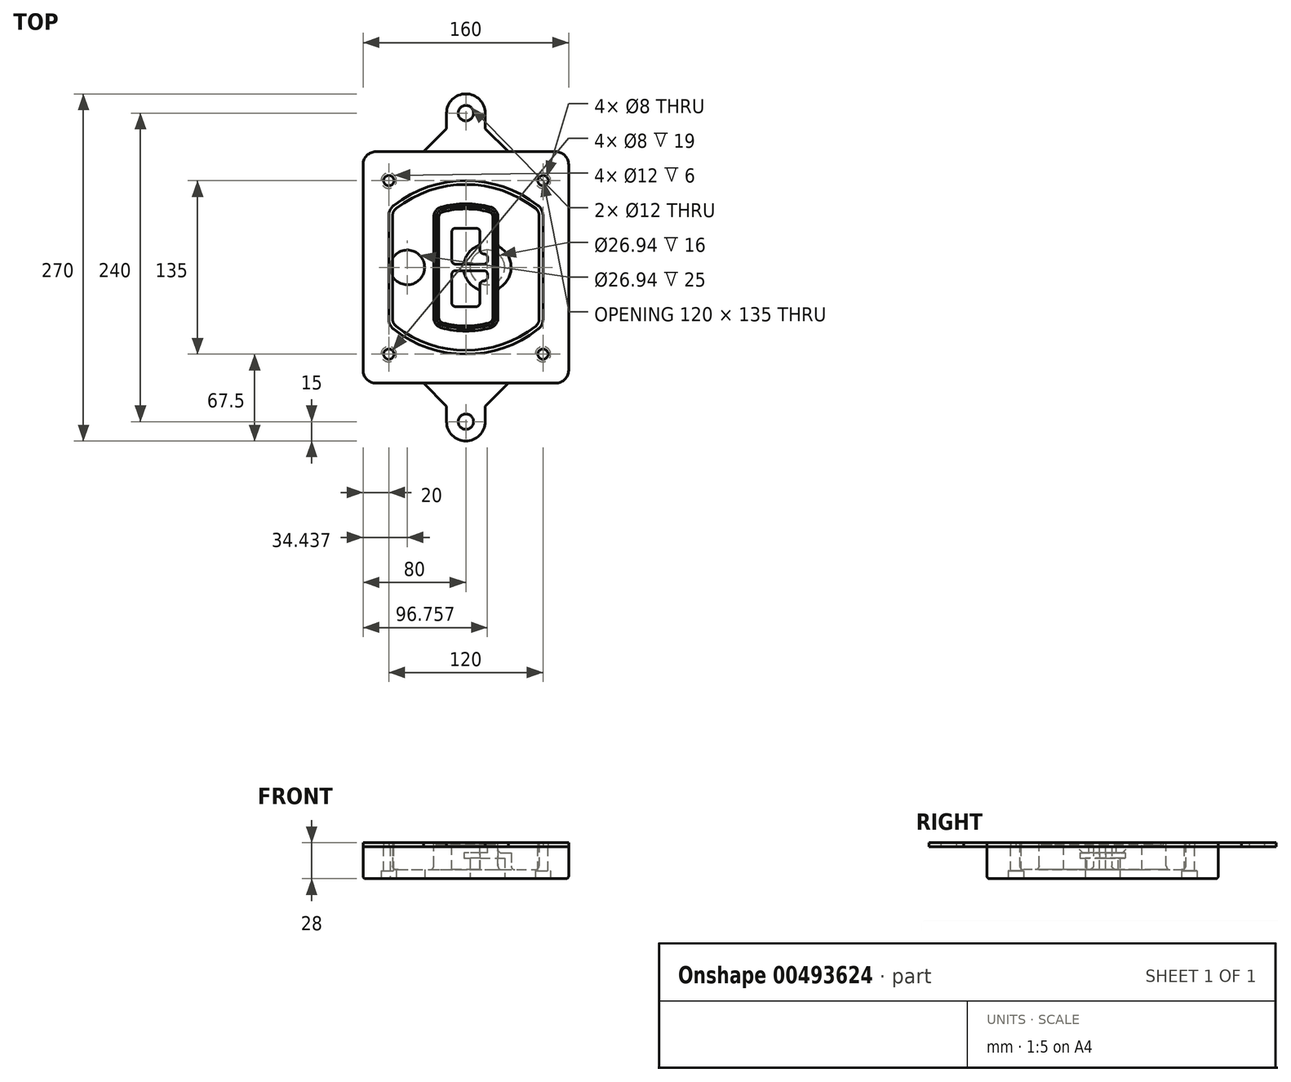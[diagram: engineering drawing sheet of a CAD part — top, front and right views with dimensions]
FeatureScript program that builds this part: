
annotation { "Feature Type Name" : "Feature", "Feature Type Description" : "" }
export const myFeature = defineFeature(function(context is Context, id is Id, definition is map)
    precondition{}
    {
        {
            var Q0;
            Q0=qCreatedBy(makeId("Top.planeOp"),FACE);
            var sketch = newSketch(context, id + "F0", { "sketchPlane" : qUnion([Q0])});
            skPoint(sketch, "E0.rect.middle", {"position": v(0, 0) * mm});
            skLineSegment(sketch, "E1.bottom", {"start": v(-70, -90) * mm, "end": v(70, -90) * mm});
            skLineSegment(sketch, "E1.top", {"start": v(-70, 90) * mm, "end": v(70, 90) * mm});
            skLineSegment(sketch, "E1.left", {"start": v(-80, -80) * mm, "end": v(-80, 80) * mm});
            skLineSegment(sketch, "E1.right", {"start": v(80, -80) * mm, "end": v(80, 80) * mm});
            skLineSegment(sketch, "E2", {"start": v(-80, 90) * mm, "end": v(80, -90) * mm, "construction": true});
            skLineSegment(sketch, "E3", {"start": v(80, 90) * mm, "end": v(-80, -90) * mm, "construction": true});
            skCircle(sketch, "E4", {"center": v(-60, 67.5) * mm, "radius": 4 * mm});
            skCircle(sketch, "E5", {"center": v(60, 67.5) * mm, "radius": 4 * mm});
            skCircle(sketch, "E6", {"center": v(60, -67.5) * mm, "radius": 4 * mm});
            skCircle(sketch, "E7", {"center": v(-60, -67.5) * mm, "radius": 4 * mm});
            skLineSegment(sketch, "E8", {"start": v(-60, 67.5) * mm, "end": v(60, 67.5) * mm, "construction": true});
            skLineSegment(sketch, "E9", {"start": v(60, 67.5) * mm, "end": v(60, -67.5) * mm, "construction": true});
            skLineSegment(sketch, "E10", {"start": v(60, -67.5) * mm, "end": v(-60, -67.5) * mm, "construction": true});
            skLineSegment(sketch, "E11", {"start": v(-60, -67.5) * mm, "end": v(-60, 67.5) * mm, "construction": true});
            skLineSegment(sketch, "E12", {"start": v(-60, 40.3) * mm, "end": v(-60, -40.3) * mm});
            skLineSegment(sketch, "E13", {"start": v(60, 40.3) * mm, "end": v(60, -40.3) * mm});
            skArc(sketch, "E14", {"start": v(56.15, 48.18) * mm, "mid": v(0, 67.5) * mm, "end": v(-56.15, 48.18) * mm});
            skArc(sketch, "E15", {"start": v(-56.15, -48.18) * mm, "mid": v(0, -67.5) * mm, "end": v(56.15, -48.18) * mm});
            skLineSegment(sketch, "E16", {"start": v(-60, 0) * mm, "end": v(60, 0) * mm, "construction": true});
            skPoint(sketch, "E17.visualSharp", {"position": v(-60, -45) * mm});
            skArc(sketch, "E17.filletArc", {"start": v(-60, -40.3) * mm, "mid": v(-58.99, -44.68) * mm, "end": v(-56.15, -48.18) * mm});
            skPoint(sketch, "E18.visualSharp", {"position": v(-60, 45) * mm});
            skArc(sketch, "E18.filletArc", {"start": v(-56.15, 48.18) * mm, "mid": v(-58.99, 44.68) * mm, "end": v(-60, 40.3) * mm});
            skPoint(sketch, "E19.visualSharp", {"position": v(60, 45) * mm});
            skArc(sketch, "E19.filletArc", {"start": v(60, 40.3) * mm, "mid": v(58.99, 44.68) * mm, "end": v(56.15, 48.18) * mm});
            skPoint(sketch, "E20.visualSharp", {"position": v(60, -45) * mm});
            skArc(sketch, "E20.filletArc", {"start": v(56.15, -48.18) * mm, "mid": v(58.99, -44.68) * mm, "end": v(60, -40.3) * mm});
            skPoint(sketch, "E21.visualSharp", {"position": v(-80, 90) * mm});
            skArc(sketch, "E21.filletArc", {"start": v(-70, 90) * mm, "mid": v(-77.07, 87.07) * mm, "end": v(-80, 80) * mm});
            skPoint(sketch, "E22.visualSharp", {"position": v(80, 90) * mm});
            skArc(sketch, "E22.filletArc", {"start": v(80, 80) * mm, "mid": v(77.07, 87.07) * mm, "end": v(70, 90) * mm});
            skPoint(sketch, "E23.visualSharp", {"position": v(80, -90) * mm});
            skArc(sketch, "E23.filletArc", {"start": v(70, -90) * mm, "mid": v(77.07, -87.07) * mm, "end": v(80, -80) * mm});
            skPoint(sketch, "E24.visualSharp", {"position": v(-80, -90) * mm});
            skArc(sketch, "E24.filletArc", {"start": v(-80, -80) * mm, "mid": v(-77.07, -87.07) * mm, "end": v(-70, -90) * mm});
            skArc(sketch, "E25.0", {"start": v(57, 40.3) * mm, "mid": v(56.3, 43.36) * mm, "end": v(54.3, 45.81) * mm});
            skLineSegment(sketch, "E25.1", {"start": v(57, 40.3) * mm, "end": v(57, -40.3) * mm});
            skArc(sketch, "E25.2", {"start": v(54.3, -45.81) * mm, "mid": v(56.3, -43.36) * mm, "end": v(57, -40.3) * mm});
            skArc(sketch, "E25.3", {"start": v(-54.3, -45.81) * mm, "mid": v(0, -64.5) * mm, "end": v(54.3, -45.81) * mm});
            skArc(sketch, "E25.4", {"start": v(-57, -40.3) * mm, "mid": v(-56.3, -43.36) * mm, "end": v(-54.3, -45.81) * mm});
            skArc(sketch, "E25.5", {"start": v(54.3, 45.81) * mm, "mid": v(0, 64.5) * mm, "end": v(-54.3, 45.81) * mm});
            skLineSegment(sketch, "E25.6", {"start": v(-57, 40.3) * mm, "end": v(-57, -40.3) * mm});
            skArc(sketch, "E25.7", {"start": v(-54.3, 45.81) * mm, "mid": v(-56.3, 43.36) * mm, "end": v(-57, 40.3) * mm});
            skArc(sketch, "E26.0", {"start": v(-58.62, 51.33) * mm, "mid": v(-62.58, 46.43) * mm, "end": v(-64, 40.3) * mm});
            skArc(sketch, "E26.1", {"start": v(58.62, 51.33) * mm, "mid": v(0, 71.5) * mm, "end": v(-58.62, 51.33) * mm});
            skArc(sketch, "E26.2", {"start": v(64, 40.3) * mm, "mid": v(62.58, 46.43) * mm, "end": v(58.62, 51.33) * mm});
            skLineSegment(sketch, "E26.3", {"start": v(64, 40.3) * mm, "end": v(64, -40.3) * mm});
            skArc(sketch, "E26.4", {"start": v(58.62, -51.33) * mm, "mid": v(62.58, -46.43) * mm, "end": v(64, -40.3) * mm});
            skLineSegment(sketch, "E26.5", {"start": v(-64, 40.3) * mm, "end": v(-64, -40.3) * mm});
            skArc(sketch, "E26.6", {"start": v(-58.62, -51.33) * mm, "mid": v(0, -71.5) * mm, "end": v(58.62, -51.33) * mm});
            skArc(sketch, "E26.7", {"start": v(-64, -40.3) * mm, "mid": v(-62.58, -46.43) * mm, "end": v(-58.62, -51.33) * mm});
            skSolve(sketch);
        }
        {
            var Q0;
            Q0=makeQuery(id+"F0.imprint","IMPRINT",FACE,{"disambiguationData":[TD([[makeQuery(id+"F0.imprint","IMPRINT",EDGE,{"derivedFrom":sQuery(id+"F0.wireOp",EDGE,"E1.bottom")}),1.0]])]});
            var Q1;
            Q1=makeQuery(id+"F0.imprint","IMPRINT",FACE,{"disambiguationData":[TD([[makeQuery(id+"F0.imprint","IMPRINT",EDGE,{"derivedFrom":sQuery(id+"F0.wireOp",EDGE,"E12")}),1.0]])]});
            var Q2;
            Q2=makeQuery(id+"F0.imprint","IMPRINT",FACE,{"disambiguationData":[TD([[makeQuery(id+"F0.imprint","IMPRINT",EDGE,{"derivedFrom":sQuery(id+"F0.wireOp",EDGE,"E25.0")}),1.0]])]});
            var Q3;
            Q3=makeQuery(id+"F0.imprint","IMPRINT",FACE,{"disambiguationData":[TD([[makeQuery(id+"F0.imprint","IMPRINT",EDGE,{"derivedFrom":sQuery(id+"F0.wireOp",EDGE,"E12")}),-1.0]])]});
            extrude(context, id + "F1", {"entities" : qUnion([Q0, Q1, Q2, Q3]), "oppositeDirection" : true, "depth" : 25 * mm});
        }
        {
            var Q0;
            Q0=makeQuery(id+"F0.imprint","IMPRINT",FACE,{"disambiguationData":[TD([[makeQuery(id+"F0.imprint","IMPRINT",EDGE,{"derivedFrom":sQuery(id+"F0.wireOp",EDGE,"E12")}),1.0]])]});
            extrude(context, id + "F2", {"entities" : qUnion([Q0]), "operationType" : NewBodyOperationType.ADD, "depth" : 3 * mm});
        }
        {
            var Q0;
            Q0=makeQuery(id+"F0.imprint","IMPRINT",FACE,{"disambiguationData":[TD([[makeQuery(id+"F0.imprint","IMPRINT",EDGE,{"derivedFrom":sQuery(id+"F0.wireOp",EDGE,"E25.0")}),1.0]])]});
            extrude(context, id + "F3", {"entities" : qUnion([Q0]), "operationType" : NewBodyOperationType.REMOVE, "oppositeDirection" : true, "depth" : 18 * mm});
        }
        {
            var Q0;
            Q0=makeQuery(id+"F2.opExtrude","CAP_FACE",FACE,{"disambiguationData":[OSD([sQuery(id+"F0.wireOp",EDGE,"E12"),sQuery(id+"F0.wireOp",EDGE,"E13"),sQuery(id+"F0.wireOp",EDGE,"E14"),sQuery(id+"F0.wireOp",EDGE,"E15"),sQuery(id+"F0.wireOp",EDGE,"E17.filletArc"),sQuery(id+"F0.wireOp",EDGE,"E18.filletArc"),sQuery(id+"F0.wireOp",EDGE,"E19.filletArc"),sQuery(id+"F0.wireOp",EDGE,"E20.filletArc"),sQuery(id+"F0.wireOp",EDGE,"E25.0"),sQuery(id+"F0.wireOp",EDGE,"E25.1"),sQuery(id+"F0.wireOp",EDGE,"E25.2"),sQuery(id+"F0.wireOp",EDGE,"E25.3"),sQuery(id+"F0.wireOp",EDGE,"E25.4"),sQuery(id+"F0.wireOp",EDGE,"E25.5"),sQuery(id+"F0.wireOp",EDGE,"E25.6"),sQuery(id+"F0.wireOp",EDGE,"E25.7")])],"isStart":false});
            var sketch = newSketch(context, id + "F4", { "sketchPlane" : qUnion([Q0])});
            skArc(sketch, "E27.0", {"start": v(-19.08, -46.97) * mm, "mid": v(0, -49.5) * mm, "end": v(19.08, -46.97) * mm});
            skArc(sketch, "E28.0", {"start": v(19.08, 46.97) * mm, "mid": v(0, 49.5) * mm, "end": v(-19.08, 46.97) * mm});
            skLineSegment(sketch, "E29", {"start": v(-25, 39.25) * mm, "end": v(-25, -39.25) * mm});
            skLineSegment(sketch, "E30", {"start": v(25, 39.25) * mm, "end": v(25, -39.25) * mm});
            skLineSegment(sketch, "E31", {"start": v(-25, 45.1) * mm, "end": v(25, 45.1) * mm, "construction": true});
            skLineSegment(sketch, "E32", {"start": v(-25, -45.1) * mm, "end": v(25, -45.1) * mm, "construction": true});
            skPoint(sketch, "E33.visualSharp", {"position": v(-25, 45.1) * mm});
            skArc(sketch, "E33.filletArc", {"start": v(-19.08, 46.97) * mm, "mid": v(-23.35, 44.11) * mm, "end": v(-25, 39.25) * mm});
            skPoint(sketch, "E34.visualSharp", {"position": v(25, 45.1) * mm});
            skArc(sketch, "E34.filletArc", {"start": v(25, 39.25) * mm, "mid": v(23.35, 44.11) * mm, "end": v(19.08, 46.97) * mm});
            skPoint(sketch, "E35.visualSharp", {"position": v(25, -45.1) * mm});
            skArc(sketch, "E35.filletArc", {"start": v(19.08, -46.97) * mm, "mid": v(23.35, -44.11) * mm, "end": v(25, -39.25) * mm});
            skPoint(sketch, "E36.visualSharp", {"position": v(-25, -45.1) * mm});
            skArc(sketch, "E36.filletArc", {"start": v(-25, -39.25) * mm, "mid": v(-23.35, -44.11) * mm, "end": v(-19.08, -46.97) * mm});
            skArc(sketch, "E37.0", {"start": v(54.3, 45.81) * mm, "mid": v(0, 64.5) * mm, "end": v(-54.3, 45.81) * mm});
            skArc(sketch, "E37.1", {"start": v(-54.3, 45.81) * mm, "mid": v(-56.3, 43.36) * mm, "end": v(-57, 40.3) * mm});
            skLineSegment(sketch, "E37.2", {"start": v(-57, 40.3) * mm, "end": v(-57, -40.3) * mm});
            skArc(sketch, "E37.3", {"start": v(-57, -40.3) * mm, "mid": v(-56.3, -43.36) * mm, "end": v(-54.3, -45.81) * mm});
            skArc(sketch, "E37.4", {"start": v(-54.3, -45.81) * mm, "mid": v(0, -64.5) * mm, "end": v(54.3, -45.81) * mm});
            skArc(sketch, "E37.5", {"start": v(54.3, -45.81) * mm, "mid": v(56.3, -43.36) * mm, "end": v(57, -40.3) * mm});
            skLineSegment(sketch, "E37.6", {"start": v(57, 40.3) * mm, "end": v(57, -40.3) * mm});
            skArc(sketch, "E37.7", {"start": v(57, 40.3) * mm, "mid": v(56.3, 43.36) * mm, "end": v(54.3, 45.81) * mm});
            skLineSegment(sketch, "E38.0", {"start": v(23, 39.25) * mm, "end": v(23, -39.25) * mm});
            skArc(sketch, "E38.1", {"start": v(18.56, -45.04) * mm, "mid": v(21.76, -42.9) * mm, "end": v(23, -39.25) * mm});
            skArc(sketch, "E38.2", {"start": v(-18.56, -45.04) * mm, "mid": v(0, -47.5) * mm, "end": v(18.56, -45.04) * mm});
            skArc(sketch, "E38.3", {"start": v(-23, -39.25) * mm, "mid": v(-21.76, -42.9) * mm, "end": v(-18.56, -45.04) * mm});
            skLineSegment(sketch, "E38.4", {"start": v(-23, 39.25) * mm, "end": v(-23, -39.25) * mm});
            skArc(sketch, "E38.5", {"start": v(23, 39.25) * mm, "mid": v(21.76, 42.9) * mm, "end": v(18.56, 45.04) * mm});
            skArc(sketch, "E38.6", {"start": v(-18.56, 45.04) * mm, "mid": v(-21.76, 42.9) * mm, "end": v(-23, 39.25) * mm});
            skArc(sketch, "E38.7", {"start": v(18.56, 45.04) * mm, "mid": v(0, 47.5) * mm, "end": v(-18.56, 45.04) * mm});
            skArc(sketch, "E39.0", {"start": v(21, 39.25) * mm, "mid": v(20.18, 41.68) * mm, "end": v(18.04, 43.1) * mm});
            skLineSegment(sketch, "E39.1", {"start": v(21, 39.25) * mm, "end": v(21, -39.25) * mm});
            skArc(sketch, "E39.2", {"start": v(18.04, -43.1) * mm, "mid": v(20.18, -41.68) * mm, "end": v(21, -39.25) * mm});
            skArc(sketch, "E39.3", {"start": v(-18.04, -43.1) * mm, "mid": v(0, -45.5) * mm, "end": v(18.04, -43.1) * mm});
            skArc(sketch, "E39.4", {"start": v(-21, -39.25) * mm, "mid": v(-20.18, -41.68) * mm, "end": v(-18.04, -43.1) * mm});
            skArc(sketch, "E39.5", {"start": v(18.04, 43.1) * mm, "mid": v(0, 45.5) * mm, "end": v(-18.04, 43.1) * mm});
            skLineSegment(sketch, "E39.6", {"start": v(-21, 39.25) * mm, "end": v(-21, -39.25) * mm});
            skArc(sketch, "E39.7", {"start": v(-18.04, 43.1) * mm, "mid": v(-20.18, 41.68) * mm, "end": v(-21, 39.25) * mm});
            skLineSegment(sketch, "E40", {"start": v(-25, 0) * mm, "end": v(25, 0) * mm, "construction": true});
            skLineSegment(sketch, "E41", {"start": v(-11, 5.5) * mm, "end": v(-11, 27.5) * mm});
            skLineSegment(sketch, "E42", {"start": v(-8, 30.5) * mm, "end": v(8, 30.5) * mm});
            skLineSegment(sketch, "E43", {"start": v(11, 27.5) * mm, "end": v(11, 13.5) * mm});
            skLineSegment(sketch, "E44", {"start": v(14, 10.5) * mm, "end": v(14, 10.5) * mm});
            skLineSegment(sketch, "E45", {"start": v(17, 7.5) * mm, "end": v(17, 5.5) * mm});
            skLineSegment(sketch, "E46", {"start": v(14, 2.5) * mm, "end": v(-8, 2.5) * mm});
            skPoint(sketch, "E47.visualSharp", {"position": v(-11, 30.5) * mm});
            skArc(sketch, "E47.filletArc", {"start": v(-8, 30.5) * mm, "mid": v(-10.12, 29.62) * mm, "end": v(-11, 27.5) * mm});
            skPoint(sketch, "E48.visualSharp", {"position": v(11, 30.5) * mm});
            skArc(sketch, "E48.filletArc", {"start": v(11, 27.5) * mm, "mid": v(10.12, 29.62) * mm, "end": v(8, 30.5) * mm});
            skPoint(sketch, "E49.visualSharp", {"position": v(11, 10.5) * mm});
            skArc(sketch, "E49.filletArc", {"start": v(11, 13.5) * mm, "mid": v(11.88, 11.38) * mm, "end": v(14, 10.5) * mm});
            skPoint(sketch, "E50.visualSharp", {"position": v(17, 10.5) * mm});
            skArc(sketch, "E50.filletArc", {"start": v(17, 7.5) * mm, "mid": v(16.12, 9.62) * mm, "end": v(14, 10.5) * mm});
            skPoint(sketch, "E51.visualSharp", {"position": v(17, 2.5) * mm});
            skArc(sketch, "E51.filletArc", {"start": v(14, 2.5) * mm, "mid": v(16.12, 3.38) * mm, "end": v(17, 5.5) * mm});
            skPoint(sketch, "E52.visualSharp", {"position": v(-11, 2.5) * mm});
            skArc(sketch, "E52.filletArc", {"start": v(-11, 5.5) * mm, "mid": v(-10.12, 3.38) * mm, "end": v(-8, 2.5) * mm});
            skLineSegment(sketch, "E53.0.MirrorCS", {"start": v(14, -2.5) * mm, "end": v(-8, -2.5) * mm});
            skArc(sketch, "E54.0.MirrorCS", {"start": v(-11, -5.5) * mm, "mid": v(-10.12, -3.38) * mm, "end": v(-8, -2.5) * mm});
            skLineSegment(sketch, "E55.0.MirrorCS", {"start": v(-11, -5.5) * mm, "end": v(-11, -27.5) * mm});
            skArc(sketch, "E56.0.MirrorCS", {"start": v(-8, -30.5) * mm, "mid": v(-10.12, -29.62) * mm, "end": v(-11, -27.5) * mm});
            skLineSegment(sketch, "E57.0.MirrorCS", {"start": v(-8, -30.5) * mm, "end": v(8, -30.5) * mm});
            skArc(sketch, "E58.0.MirrorCS", {"start": v(11, -27.5) * mm, "mid": v(10.12, -29.62) * mm, "end": v(8, -30.5) * mm});
            skLineSegment(sketch, "E59.0.MirrorCS", {"start": v(11, -27.5) * mm, "end": v(11, -13.5) * mm});
            skArc(sketch, "E60.0.MirrorCS", {"start": v(11, -13.5) * mm, "mid": v(11.88, -11.38) * mm, "end": v(14, -10.5) * mm});
            skArc(sketch, "E61.0.MirrorCS", {"start": v(17, -7.5) * mm, "mid": v(16.12, -9.62) * mm, "end": v(14, -10.5) * mm});
            skLineSegment(sketch, "E62.0.MirrorCS", {"start": v(17, -7.5) * mm, "end": v(17, -5.5) * mm});
            skArc(sketch, "E63.0.MirrorCS", {"start": v(14, -2.5) * mm, "mid": v(16.12, -3.38) * mm, "end": v(17, -5.5) * mm});
            skSolve(sketch);
        }
        {
            var Q0;
            Q0=makeQuery(id+"F4.imprint","IMPRINT",FACE,{"disambiguationData":[TD([[makeQuery(id+"F4.imprint","IMPRINT",EDGE,{"derivedFrom":sQuery(id+"F4.wireOp",EDGE,"E27.0")}),1.0]])]});
            var Q1;
            Q1=makeQuery(id+"F4.imprint","IMPRINT",FACE,{"disambiguationData":[TD([[makeQuery(id+"F4.imprint","IMPRINT",EDGE,{"derivedFrom":sQuery(id+"F4.wireOp",EDGE,"E38.0")}),-1.0]])]});
            var Q2;
            Q2=makeQuery(id+"F4.imprint","IMPRINT",FACE,{"disambiguationData":[TD([[makeQuery(id+"F4.imprint","IMPRINT",EDGE,{"derivedFrom":sQuery(id+"F4.wireOp",EDGE,"E39.0")}),1.0]])]});
            extrude(context, id + "F5", {"entities" : qUnion([Q0, Q1, Q2]), "operationType" : NewBodyOperationType.ADD, "endBound" : BoundingType.UP_TO_NEXT, "oppositeDirection" : true, "depth" : 25 * mm});
        }
        {
            var Q0;
            Q0=makeQuery(id+"F4.imprint","IMPRINT",FACE,{"disambiguationData":[TD([[makeQuery(id+"F4.imprint","IMPRINT",EDGE,{"derivedFrom":sQuery(id+"F4.wireOp",EDGE,"E38.0")}),-1.0]])]});
            extrude(context, id + "F6", {"entities" : qUnion([Q0]), "operationType" : NewBodyOperationType.REMOVE, "oppositeDirection" : true, "depth" : 2 * mm});
        }
        {
            var Q0;
            Q0=makeQuery(id+"F1.opExtrude","CAP_FACE",FACE,{"disambiguationData":[OSD([sQuery(id+"F0.wireOp",EDGE,"E1.bottom"),sQuery(id+"F0.wireOp",EDGE,"E1.top"),sQuery(id+"F0.wireOp",EDGE,"E1.left"),sQuery(id+"F0.wireOp",EDGE,"E1.right"),sQuery(id+"F0.wireOp",EDGE,"E4"),sQuery(id+"F0.wireOp",EDGE,"E5"),sQuery(id+"F0.wireOp",EDGE,"E6"),sQuery(id+"F0.wireOp",EDGE,"E7"),sQuery(id+"F0.wireOp",EDGE,"E21.filletArc"),sQuery(id+"F0.wireOp",EDGE,"E22.filletArc"),sQuery(id+"F0.wireOp",EDGE,"E23.filletArc"),sQuery(id+"F0.wireOp",EDGE,"E24.filletArc")])],"isStart":false});
            var sketch = newSketch(context, id + "F7", { "sketchPlane" : qUnion([Q0])});
            skCircle(sketch, "E64", {"center": v(16.76, 0) * mm, "radius": 13.47 * mm});
            skCircle(sketch, "E65", {"center": v(-45.56, 0) * mm, "radius": 13.47 * mm});
            skLineSegment(sketch, "E66", {"start": v(80, 0) * mm, "end": v(-80, 0) * mm});
            skCircle(sketch, "E67", {"center": v(16.76, 0) * mm, "radius": 18.47 * mm});
            skCircle(sketch, "E68", {"center": v(60, -67.5) * mm, "radius": 6 * mm});
            skCircle(sketch, "E69", {"center": v(-60, -67.5) * mm, "radius": 6 * mm});
            skCircle(sketch, "E70", {"center": v(-60, 67.5) * mm, "radius": 6 * mm});
            skCircle(sketch, "E71", {"center": v(60, 67.5) * mm, "radius": 6 * mm});
            skSolve(sketch);
        }
        {
            var Q0;
            {var subQ1=sQuery(id+"F7.wireOp",EDGE,"E66");var subQ4=sQuery(id+"F7.wireOp",EDGE,"E64");var subQ6=makeQuery(id+"F7.imprint","INTERSECT",VERTEX,{"disambiguationData":[OD(0.0)],"derivedFrom":[subQ4,subQ1]});Q0=makeQuery(id+"F7.imprint","IMPRINT",FACE,{"disambiguationData":[TD([[makeQuery(id+"F7.imprint","IMPRINT",EDGE,{"disambiguationData":[TD([[subQ6,-1.0]])],"derivedFrom":subQ4}),-1.0]])]});}
            var Q1;
            {var subQ0=sQuery(id+"F7.wireOp",EDGE,"E66");var subQ1=sQuery(id+"F7.wireOp",EDGE,"E64");var subQ3=makeQuery(id+"F7.imprint","INTERSECT",VERTEX,{"disambiguationData":[OD(0.0)],"derivedFrom":[subQ1,subQ0]});Q1=makeQuery(id+"F7.imprint","IMPRINT",FACE,{"disambiguationData":[TD([[makeQuery(id+"F7.imprint","IMPRINT",EDGE,{"disambiguationData":[TD([[subQ3,-1.0]])],"derivedFrom":subQ1}),1.0]])]});}
            var Q2;
            {var subQ0=sQuery(id+"F7.wireOp",EDGE,"E66");var subQ1=sQuery(id+"F7.wireOp",EDGE,"E64");var subQ3=makeQuery(id+"F7.imprint","INTERSECT",VERTEX,{"disambiguationData":[OD(0.0)],"derivedFrom":[subQ1,subQ0]});Q2=makeQuery(id+"F7.imprint","IMPRINT",FACE,{"disambiguationData":[TD([[makeQuery(id+"F7.imprint","IMPRINT",EDGE,{"disambiguationData":[TD([[subQ3,1.0]])],"derivedFrom":subQ1}),1.0]])]});}
            var Q3;
            {var subQ1=sQuery(id+"F7.wireOp",EDGE,"E66");var subQ4=sQuery(id+"F7.wireOp",EDGE,"E64");var subQ6=makeQuery(id+"F7.imprint","INTERSECT",VERTEX,{"disambiguationData":[OD(0.0)],"derivedFrom":[subQ4,subQ1]});Q3=makeQuery(id+"F7.imprint","IMPRINT",FACE,{"disambiguationData":[TD([[makeQuery(id+"F7.imprint","IMPRINT",EDGE,{"disambiguationData":[TD([[subQ6,1.0]])],"derivedFrom":subQ4}),-1.0]])]});}
            extrude(context, id + "F8", {"entities" : qUnion([Q0, Q1, Q2, Q3]), "operationType" : NewBodyOperationType.ADD, "oppositeDirection" : true, "depth" : 20 * mm});
        }
        {
            var Q0;
            {var subQ0=sQuery(id+"F7.wireOp",EDGE,"E66");var subQ1=sQuery(id+"F7.wireOp",EDGE,"E64");var subQ3=makeQuery(id+"F7.imprint","INTERSECT",VERTEX,{"disambiguationData":[OD(0.0)],"derivedFrom":[subQ1,subQ0]});Q0=makeQuery(id+"F7.imprint","IMPRINT",FACE,{"disambiguationData":[TD([[makeQuery(id+"F7.imprint","IMPRINT",EDGE,{"disambiguationData":[TD([[subQ3,-1.0]])],"derivedFrom":subQ1}),1.0]])]});}
            var Q1;
            {var subQ0=sQuery(id+"F7.wireOp",EDGE,"E66");var subQ1=sQuery(id+"F7.wireOp",EDGE,"E64");var subQ3=makeQuery(id+"F7.imprint","INTERSECT",VERTEX,{"disambiguationData":[OD(0.0)],"derivedFrom":[subQ1,subQ0]});Q1=makeQuery(id+"F7.imprint","IMPRINT",FACE,{"disambiguationData":[TD([[makeQuery(id+"F7.imprint","IMPRINT",EDGE,{"disambiguationData":[TD([[subQ3,1.0]])],"derivedFrom":subQ1}),1.0]])]});}
            extrude(context, id + "F9", {"entities" : qUnion([Q0, Q1]), "operationType" : NewBodyOperationType.REMOVE, "oppositeDirection" : true, "depth" : 16 * mm});
        }
        {
            var Q0;
            {var subQ0=sQuery(id+"F7.wireOp",EDGE,"E66");var subQ1=sQuery(id+"F7.wireOp",EDGE,"E65");var subQ3=makeQuery(id+"F7.imprint","INTERSECT",VERTEX,{"disambiguationData":[OD(0.0)],"derivedFrom":[subQ1,subQ0]});Q0=makeQuery(id+"F7.imprint","IMPRINT",FACE,{"disambiguationData":[TD([[makeQuery(id+"F7.imprint","IMPRINT",EDGE,{"disambiguationData":[TD([[subQ3,-1.0]])],"derivedFrom":subQ1}),1.0]])]});}
            var Q1;
            {var subQ0=sQuery(id+"F7.wireOp",EDGE,"E66");var subQ1=sQuery(id+"F7.wireOp",EDGE,"E65");var subQ3=makeQuery(id+"F7.imprint","INTERSECT",VERTEX,{"disambiguationData":[OD(0.0)],"derivedFrom":[subQ1,subQ0]});Q1=makeQuery(id+"F7.imprint","IMPRINT",FACE,{"disambiguationData":[TD([[makeQuery(id+"F7.imprint","IMPRINT",EDGE,{"disambiguationData":[TD([[subQ3,1.0]])],"derivedFrom":subQ1}),1.0]])]});}
            extrude(context, id + "F10", {"entities" : qUnion([Q0, Q1]), "operationType" : NewBodyOperationType.REMOVE, "oppositeDirection" : true, "depth" : 25 * mm});
        }
        {
            var Q0;
            Q0=makeQuery(id+"F7.imprint","IMPRINT",FACE,{"disambiguationData":[TD([[makeQuery(id+"F7.imprint","IMPRINT",EDGE,{"derivedFrom":sQuery(id+"F7.wireOp",EDGE,"E68")}),1.0]])]});
            var Q1;
            Q1=makeQuery(id+"F7.imprint","IMPRINT",FACE,{"disambiguationData":[TD([[makeQuery(id+"F7.imprint","IMPRINT",EDGE,{"derivedFrom":makeQuery(id+"F1.opExtrude","CAP_EDGE",EDGE,{"disambiguationData":[OSD([sQuery(id+"F0.wireOp",EDGE,"E5")])],"isStart":false})}),-1.0]])]});
            var Q2;
            Q2=makeQuery(id+"F7.imprint","IMPRINT",FACE,{"disambiguationData":[TD([[makeQuery(id+"F7.imprint","IMPRINT",EDGE,{"derivedFrom":sQuery(id+"F7.wireOp",EDGE,"E69")}),1.0]])]});
            var Q3;
            Q3=makeQuery(id+"F7.imprint","IMPRINT",FACE,{"disambiguationData":[TD([[makeQuery(id+"F7.imprint","IMPRINT",EDGE,{"derivedFrom":makeQuery(id+"F1.opExtrude","CAP_EDGE",EDGE,{"disambiguationData":[OSD([sQuery(id+"F0.wireOp",EDGE,"E4")])],"isStart":false})}),-1.0]])]});
            var Q4;
            Q4=makeQuery(id+"F7.imprint","IMPRINT",FACE,{"disambiguationData":[TD([[makeQuery(id+"F7.imprint","IMPRINT",EDGE,{"derivedFrom":sQuery(id+"F7.wireOp",EDGE,"E70")}),1.0]])]});
            var Q5;
            Q5=makeQuery(id+"F7.imprint","IMPRINT",FACE,{"disambiguationData":[TD([[makeQuery(id+"F7.imprint","IMPRINT",EDGE,{"derivedFrom":makeQuery(id+"F1.opExtrude","CAP_EDGE",EDGE,{"disambiguationData":[OSD([sQuery(id+"F0.wireOp",EDGE,"E7")])],"isStart":false})}),-1.0]])]});
            var Q6;
            Q6=makeQuery(id+"F7.imprint","IMPRINT",FACE,{"disambiguationData":[TD([[makeQuery(id+"F7.imprint","IMPRINT",EDGE,{"derivedFrom":sQuery(id+"F7.wireOp",EDGE,"E71")}),1.0]])]});
            var Q7;
            Q7=makeQuery(id+"F7.imprint","IMPRINT",FACE,{"disambiguationData":[TD([[makeQuery(id+"F7.imprint","IMPRINT",EDGE,{"derivedFrom":makeQuery(id+"F1.opExtrude","CAP_EDGE",EDGE,{"disambiguationData":[OSD([sQuery(id+"F0.wireOp",EDGE,"E6")])],"isStart":false})}),-1.0]])]});
            extrude(context, id + "F11", {"entities" : qUnion([Q0, Q1, Q2, Q3, Q4, Q5, Q6, Q7]), "operationType" : NewBodyOperationType.REMOVE, "oppositeDirection" : true, "depth" : 6 * mm});
        }
        {
            var Q0;
            Q0=makeQuery(id+"F9.boolean.opBoolean","COPY",FACE,{"derivedFrom":makeQuery(id+"F9.opExtrude","CAP_FACE",FACE,{"disambiguationData":[OSD([sQuery(id+"F7.wireOp",EDGE,"E64")])],"isStart":false})});
            var sketch = newSketch(context, id + "F12", { "sketchPlane" : qUnion([Q0])});
            skArc(sketch, "E72.0", {"start": v(11, 17.55) * mm, "mid": v(2.57, 11.82) * mm, "end": v(-1.54, 2.5) * mm});
            skArc(sketch, "E72.1", {"start": v(-1.54, -2.5) * mm, "mid": v(2.57, -11.82) * mm, "end": v(11, -17.55) * mm});
            skLineSegment(sketch, "E73", {"start": v(-1.54, -2.5) * mm, "end": v(14, -2.5) * mm});
            skLineSegment(sketch, "E74.0", {"start": v(14, 2.5) * mm, "end": v(-1.54, 2.5) * mm});
            skArc(sketch, "E74.1", {"start": v(14, 2.5) * mm, "mid": v(16.12, 3.38) * mm, "end": v(17, 5.5) * mm});
            skLineSegment(sketch, "E74.2", {"start": v(17, 7.5) * mm, "end": v(17, 5.5) * mm});
            skArc(sketch, "E74.3", {"start": v(17, 7.5) * mm, "mid": v(16.12, 9.62) * mm, "end": v(14, 10.5) * mm});
            skArc(sketch, "E74.4", {"start": v(11, 13.5) * mm, "mid": v(11.88, 11.38) * mm, "end": v(14, 10.5) * mm});
            skLineSegment(sketch, "E74.5", {"start": v(11, 17.55) * mm, "end": v(11, 13.5) * mm});
            skLineSegment(sketch, "E74.7", {"start": v(14, -2.5) * mm, "end": v(-1.54, -2.5) * mm});
            skArc(sketch, "E74.8", {"start": v(14, -2.5) * mm, "mid": v(16.12, -3.38) * mm, "end": v(17, -5.5) * mm});
            skLineSegment(sketch, "E74.9", {"start": v(17, -7.5) * mm, "end": v(17, -5.5) * mm});
            skArc(sketch, "E74.10", {"start": v(17, -7.5) * mm, "mid": v(16.12, -9.62) * mm, "end": v(14, -10.5) * mm});
            skArc(sketch, "E74.11", {"start": v(11, -13.5) * mm, "mid": v(11.88, -11.38) * mm, "end": v(14, -10.5) * mm});
            skLineSegment(sketch, "E74.12", {"start": v(11, -17.55) * mm, "end": v(11, -13.5) * mm});
            skPoint(sketch, "E75.orphan", {"position": v(11, -27.5) * mm});
            skPoint(sketch, "E76.orphan", {"position": v(-8, -2.5) * mm});
            skPoint(sketch, "E77.orphan", {"position": v(-8, 2.5) * mm});
            skPoint(sketch, "E78.orphan", {"position": v(11, 27.5) * mm});
            skSolve(sketch);
        }
        {
            var Q0;
            {var subQ7=sQuery(id+"F12.wireOp",EDGE,"E72.0");var subQ14=sQuery(id+"F12.wireOp",EDGE,"E72.1");var subQ16=sQuery(id+"F12.wireOp",EDGE,"E74.1");var subQ18=sQuery(id+"F12.wireOp",EDGE,"E74.8");Q0=qUnion([makeQuery(id+"F12.imprint","IMPRINT",FACE,{"disambiguationData":[TD([[makeQuery(id+"F12.imprint","IMPRINT",EDGE,{"derivedFrom":subQ7}),1.0]])]}),makeQuery(id+"F12.imprint","IMPRINT",FACE,{"disambiguationData":[TD([[makeQuery(id+"F12.imprint","IMPRINT",EDGE,{"derivedFrom":subQ14}),1.0]])]}),makeQuery(id+"F12.imprint","IMPRINT",FACE,{"disambiguationData":[TD([[makeQuery(id+"F12.imprint","IMPRINT",EDGE,{"derivedFrom":subQ16}),1.0]])]}),makeQuery(id+"F12.imprint","IMPRINT",FACE,{"disambiguationData":[TD([[makeQuery(id+"F12.imprint","IMPRINT",EDGE,{"derivedFrom":subQ18}),-1.0]])]})]);}
            var Q1;
            Q1=makeQuery(id+"F5.boolean.opBoolean","SPLIT",FACE,{"disambiguationData":[TD([makeQuery(id+"F5.opExtrude","SWEPT_FACE",FACE,{"disambiguationData":[OSD([sQuery(id+"F4.wireOp",EDGE,"E41")])]})])],"derivedFrom":makeQuery(id+"F3.boolean.opBoolean","COPY",FACE,{"derivedFrom":makeQuery(id+"F3.opExtrude","CAP_FACE",FACE,{"disambiguationData":[OSD([sQuery(id+"F0.wireOp",EDGE,"E25.0"),sQuery(id+"F0.wireOp",EDGE,"E25.1"),sQuery(id+"F0.wireOp",EDGE,"E25.2"),sQuery(id+"F0.wireOp",EDGE,"E25.3"),sQuery(id+"F0.wireOp",EDGE,"E25.4"),sQuery(id+"F0.wireOp",EDGE,"E25.5"),sQuery(id+"F0.wireOp",EDGE,"E25.6"),sQuery(id+"F0.wireOp",EDGE,"E25.7")])],"isStart":false})})});
            extrude(context, id + "F13", {"entities" : qUnion([Q0]), "operationType" : NewBodyOperationType.REMOVE, "endBound" : BoundingType.UP_TO_SURFACE, "endBoundEntityFace" : qUnion([Q1]), "depth" : 25 * mm});
        }
        {
            var Q0;
            Q0=makeQuery(id+"F3.boolean.opBoolean","COPY",EDGE,{"derivedFrom":makeQuery(id+"F3.opExtrude","CAP_EDGE",EDGE,{"disambiguationData":[OSD([sQuery(id+"F0.wireOp",EDGE,"E25.6")])],"isStart":false})});
            var Q1;
            Q1=makeQuery(id+"F8.boolean.opBoolean","INTERSECT",EDGE,{"derivedFrom":[makeQuery(id+"F5.opExtrude","SWEPT_FACE",FACE,{"disambiguationData":[OSD([sQuery(id+"F4.wireOp",EDGE,"E30")])]}),makeQuery(id+"F8.opExtrude","CAP_FACE",FACE,{"disambiguationData":[OSD([sQuery(id+"F7.wireOp",EDGE,"E67")])],"isStart":false})]});
            var Q2;
            Q2=makeQuery(id+"F8.boolean.opBoolean","INTERSECT",EDGE,{"disambiguationData":[OD(1.0)],"derivedFrom":[makeQuery(id+"F5.opExtrude","SWEPT_FACE",FACE,{"disambiguationData":[OSD([sQuery(id+"F4.wireOp",EDGE,"E30")])]}),makeQuery(id+"F8.opExtrude","SWEPT_FACE",FACE,{"disambiguationData":[OSD([sQuery(id+"F7.wireOp",EDGE,"E67")])]})]});
            var Q3;
            {var subQ0=sQuery(id+"F4.wireOp",EDGE,"E30");Q3=makeQuery(id+"F8.boolean.opBoolean","SPLIT",EDGE,{"disambiguationData":[TD([makeQuery(id+"F5.opExtrude","SWEPT_FACE",FACE,{"disambiguationData":[OSD([sQuery(id+"F4.wireOp",EDGE,"E35.filletArc")])]})])],"derivedFrom":makeQuery(id+"F5.opExtrude","CAP_EDGE",EDGE,{"disambiguationData":[OSD([subQ0])],"isStart":false})});}
            var Q4;
            {var subQ0=sQuery(id+"F0.wireOp",EDGE,"E25.7");var subQ1=sQuery(id+"F0.wireOp",EDGE,"E25.1");var subQ2=sQuery(id+"F0.wireOp",EDGE,"E25.6");var subQ3=sQuery(id+"F0.wireOp",EDGE,"E25.5");var subQ4=sQuery(id+"F0.wireOp",EDGE,"E25.4");var subQ5=sQuery(id+"F0.wireOp",EDGE,"E25.0");var subQ6=sQuery(id+"F0.wireOp",EDGE,"E25.2");var subQ7=sQuery(id+"F0.wireOp",EDGE,"E25.3");Q4=makeQuery(id+"F8.boolean.opBoolean","INTERSECT",EDGE,{"derivedFrom":[makeQuery(id+"F5.boolean.opBoolean","SPLIT",FACE,{"disambiguationData":[TD([makeQuery(id+"F2.opExtrude","SWEPT_FACE",FACE,{"disambiguationData":[OSD([subQ5])]})])],"derivedFrom":makeQuery(id+"F3.boolean.opBoolean","COPY",FACE,{"derivedFrom":makeQuery(id+"F3.opExtrude","CAP_FACE",FACE,{"disambiguationData":[OSD([subQ5,subQ1,subQ6,subQ7,subQ4,subQ3,subQ2,subQ0])],"isStart":false})})}),makeQuery(id+"F8.opExtrude","SWEPT_FACE",FACE,{"disambiguationData":[OSD([sQuery(id+"F7.wireOp",EDGE,"E67")])]})]});}
            var Q5;
            Q5=makeQuery(id+"F8.boolean.opBoolean","INTERSECT",EDGE,{"disambiguationData":[OD(0.0)],"derivedFrom":[makeQuery(id+"F5.opExtrude","SWEPT_FACE",FACE,{"disambiguationData":[OSD([sQuery(id+"F4.wireOp",EDGE,"E30")])]}),makeQuery(id+"F8.opExtrude","SWEPT_FACE",FACE,{"disambiguationData":[OSD([sQuery(id+"F7.wireOp",EDGE,"E67")])]})]});
            fillet(context, id + "F14", {"entities" : qUnion([Q0, Q1, Q2, Q3, Q4, Q5]), "radius" : 3 * mm, "tangentPropagation" : true, "allowEdgeOverflow" : false});
        }
        {
            var Q0;
            Q0=makeQuery(id+"F1.opExtrude","CAP_EDGE",EDGE,{"disambiguationData":[OSD([sQuery(id+"F0.wireOp",EDGE,"E1.bottom")])],"isStart":false});
            fillet(context, id + "F15", {"entities" : qUnion([Q0]), "radius" : 2 * mm, "tangentPropagation" : true, "allowEdgeOverflow" : false});
        }
        {
            var Q0;
            Q0=makeQuery(id+"F0.imprint","IMPRINT",FACE,{"disambiguationData":[TD([[makeQuery(id+"F0.imprint","IMPRINT",EDGE,{"derivedFrom":sQuery(id+"F0.wireOp",EDGE,"E1.bottom")}),1.0]])]});
            var sketch = newSketch(context, id + "F16", { "sketchPlane" : qUnion([Q0])});
            skLineSegment(sketch, "E79", {"start": v(0, 90) * mm, "end": v(0, 120) * mm, "construction": true});
            skCircle(sketch, "E80", {"center": v(0, 120) * mm, "radius": 6 * mm});
            skLineSegment(sketch, "E81", {"start": v(-33, 90) * mm, "end": v(-15, 108) * mm});
            skLineSegment(sketch, "E82", {"start": v(-15, 108) * mm, "end": v(-15, 120) * mm});
            skLineSegment(sketch, "E83", {"start": v(33, 90) * mm, "end": v(15, 108) * mm});
            skLineSegment(sketch, "E84", {"start": v(15, 108) * mm, "end": v(15, 120) * mm});
            skArc(sketch, "E85", {"start": v(15, 120) * mm, "mid": v(0, 135) * mm, "end": v(-15, 120) * mm});
            skLineSegment(sketch, "E86", {"start": v(80, 0) * mm, "end": v(-80, 0) * mm, "construction": true});
            skLineSegment(sketch, "E87.MirrorCS", {"start": v(15, -108) * mm, "end": v(15, -120) * mm});
            skLineSegment(sketch, "E88.MirrorCS", {"start": v(-15, -108) * mm, "end": v(-15, -120) * mm});
            skLineSegment(sketch, "E89.MirrorCS", {"start": v(33, -90) * mm, "end": v(15, -108) * mm});
            skArc(sketch, "E90.MirrorCS", {"start": v(15, -120) * mm, "mid": v(0, -135) * mm, "end": v(-15, -120) * mm});
            skCircle(sketch, "E91.MirrorC", {"center": v(0, -120) * mm, "radius": 6 * mm});
            skLineSegment(sketch, "E92.MirrorCS", {"start": v(0, -90) * mm, "end": v(0, -120) * mm, "construction": true});
            skLineSegment(sketch, "E93.MirrorCS", {"start": v(-33, -90) * mm, "end": v(-15, -108) * mm});
            skLineSegment(sketch, "E94", {"start": v(-33, 90) * mm, "end": v(33, 90) * mm});
            skLineSegment(sketch, "E95", {"start": v(-33, -90) * mm, "end": v(33, -90) * mm});
            skSolve(sketch);
        }
        {
            var Q0;
            Q0 = qSketchRegion(id + "F16", true);
            var Q1;
            Q1=makeQuery(id+"F0.imprint","IMPRINT",FACE,{"disambiguationData":[TD([[makeQuery(id+"F0.imprint","IMPRINT",EDGE,{"derivedFrom":sQuery(id+"F0.wireOp",EDGE,"E12")}),-1.0]])]});
            var Q2;
            Q2=makeQuery(id+"F0.imprint","IMPRINT",FACE,{"disambiguationData":[TD([[makeQuery(id+"F0.imprint","IMPRINT",EDGE,{"derivedFrom":sQuery(id+"F0.wireOp",EDGE,"E1.bottom")}),1.0]])]});
            var Q3;
            Q3=makeQuery(id+"F2.opExtrude","CAP_FACE",FACE,{"disambiguationData":[OSD([sQuery(id+"F0.wireOp",EDGE,"E12"),sQuery(id+"F0.wireOp",EDGE,"E13"),sQuery(id+"F0.wireOp",EDGE,"E14"),sQuery(id+"F0.wireOp",EDGE,"E15"),sQuery(id+"F0.wireOp",EDGE,"E17.filletArc"),sQuery(id+"F0.wireOp",EDGE,"E18.filletArc"),sQuery(id+"F0.wireOp",EDGE,"E19.filletArc"),sQuery(id+"F0.wireOp",EDGE,"E20.filletArc"),sQuery(id+"F0.wireOp",EDGE,"E25.0"),sQuery(id+"F0.wireOp",EDGE,"E25.1"),sQuery(id+"F0.wireOp",EDGE,"E25.2"),sQuery(id+"F0.wireOp",EDGE,"E25.3"),sQuery(id+"F0.wireOp",EDGE,"E25.4"),sQuery(id+"F0.wireOp",EDGE,"E25.5"),sQuery(id+"F0.wireOp",EDGE,"E25.6"),sQuery(id+"F0.wireOp",EDGE,"E25.7")])],"isStart":false});
            extrude(context, id + "F17", {"entities" : qUnion([Q0, Q1, Q2]), "endBound" : BoundingType.UP_TO_SURFACE, "endBoundEntityFace" : qUnion([Q3]), "depth" : 25 * mm});
        }
    });
